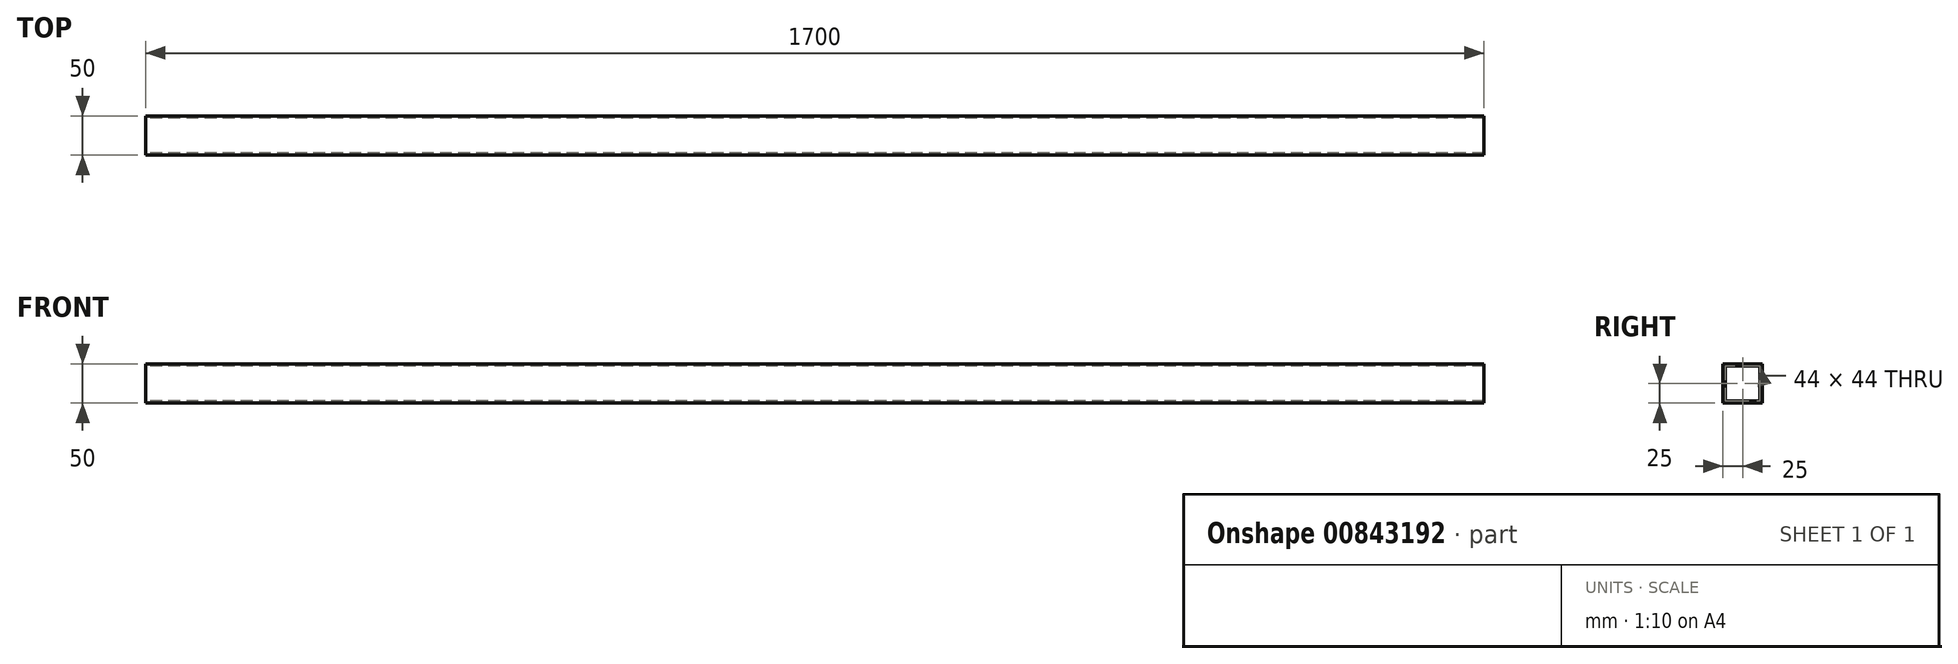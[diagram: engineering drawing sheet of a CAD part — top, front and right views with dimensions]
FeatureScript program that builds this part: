
annotation { "Feature Type Name" : "Feature", "Feature Type Description" : "" }
export const myFeature = defineFeature(function(context is Context, id is Id, definition is map)
    precondition{}
    {
        {
            var Q0;
            Q0=qCreatedBy(makeId("Right.planeOp"),FACE);
            var sketch = newSketch(context, id + "F0", { "sketchPlane" : qUnion([Q0])});
            skLineSegment(sketch, "E0.bottom", {"start": v(25, -25) * mm, "end": v(-25, -25) * mm});
            skLineSegment(sketch, "E0.top", {"start": v(25, 25) * mm, "end": v(-25, 25) * mm});
            skLineSegment(sketch, "E0.left", {"start": v(25, -25) * mm, "end": v(25, 25) * mm});
            skLineSegment(sketch, "E0.right", {"start": v(-25, -25) * mm, "end": v(-25, 25) * mm});
            skPoint(sketch, "E0.middle", {"position": v(0, 0) * mm});
            skLineSegment(sketch, "E1.0", {"start": v(22, 22) * mm, "end": v(-22, 22) * mm});
            skLineSegment(sketch, "E1.1", {"start": v(22, -22) * mm, "end": v(22, 22) * mm});
            skLineSegment(sketch, "E1.2", {"start": v(22, -22) * mm, "end": v(-22, -22) * mm});
            skLineSegment(sketch, "E1.3", {"start": v(-22, -22) * mm, "end": v(-22, 22) * mm});
            skSolve(sketch);
        }
        {
            var Q0;
            Q0=qSketchRegion(id+"F0",true);
            extrude(context, id + "F1", {"entities" : qUnion([Q0]), "depth" : 1700 * mm, "offsetDistance" : 25 * mm});
        }
    });
